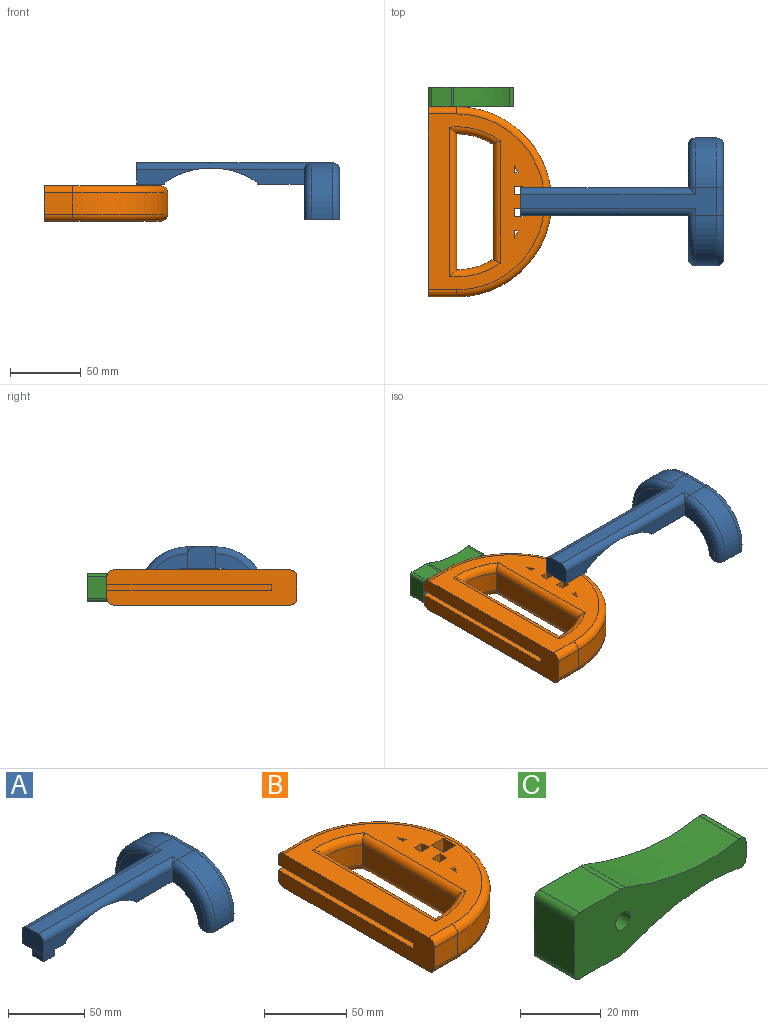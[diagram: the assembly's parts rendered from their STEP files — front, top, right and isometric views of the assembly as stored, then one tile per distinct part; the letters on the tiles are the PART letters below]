
ASSEMBLY  parts=3 mates=2
PART A: 36 faces, bbox 143.8x96.2x43.9 mm
  f0: plane 20x19.96mm, normal (0,0,-1), area 299.2mm2, adj f1,f2,f3,f7,f31,f32,f33,f34
  f1: plane 40.31x10mm, normal (0,1,0), area 274.9mm2, adj f0,f3,f7,f18,f28
  f2: plane 40.31x10mm, normal (0,-1,0), area 274.9mm2, adj f0,f3,f7,f18,f25
  f3: plane 20x1mm, normal (1,0,0), area 20mm2, adj f0,f1,f2,f18
  f4: plane 53.52x10mm, normal (0,-1,0), area 407mm2, adj f6,f11,f18,f19,f25
  f5: plane 53.52x10mm, normal (0,1,0), area 407mm2, adj f6,f17,f18,f19,f28
  f6: plane 58.17x20mm, normal (0,0,-1), area 1163.4mm2, adj f4,f5,f8,f12,f14,f19
  f7: plane 20x15mm, normal (-1,0,0), area 289.3mm2, adj f0,f1,f2,f9,f25,f28
  f8: plane 80.39x34.78mm, normal (1,0,0), area 932.2mm2, adj f6,f10,f12,f14,f15,f20,f21,f22
  f9: plane 138.77x20mm, normal (0,0,1), area 1537.7mm2, adj f7,f13,f16,f21,f25,f26,f28,f29
  f10: plane 25x5.44mm, normal (0,0,-1), area 125.2mm2, adj f8,f11,f13,f20,f24,f27
  f11: plane 34.78x30.2mm, normal (-1,0,0), area 366.1mm2, adj f4,f10,f12,f24,f27
  f12: cylinder r=24.9mm len=25mm, axis (1,0,0), area 870.7mm2, adj f6,f8,f11,f24
  f13: cylinder r=35.2mm len=39.78mm, axis (1,0,0), area 898.3mm2, adj f9,f10,f20,f27
  f14: cylinder r=24.9mm len=25mm, axis (1,0,0), area 870.7mm2, adj f6,f8,f17,f23
  f15: plane 25x5.44mm, normal (0,0,-1), area 125.2mm2, adj f8,f16,f17,f22,f23,f30
  f16: cylinder r=35.2mm len=39.78mm, axis (1,0,0), area 898.3mm2, adj f9,f15,f22,f30
  f17: plane 34.78x30.2mm, normal (-1,0,0), area 366.1mm2, adj f5,f14,f15,f23,f30
  f18: cylinder r=57.08mm len=65.64mm, axis (0,1,0), area 1393.5mm2, adj f1,f2,f3,f4,f5,f19,f25,f28
  f19: plane 20x1mm, normal (-1,0,0), area 20mm2, adj f4,f5,f6,f18
  f20: torus R=30.2mm, axis (1,0,0), area 448mm2, adj f8,f10,f13,f21
  f21: cylinder r=5mm len=20mm, axis (0,-1,0), area 157.1mm2, adj f8,f9,f20,f22
  f22: torus R=30.2mm, axis (1,0,0), area 448mm2, adj f8,f15,f16,f21
  f23: cylinder r=5mm len=25mm, axis (1,0,0), area 174.9mm2, adj f8,f14,f15,f17
  f24: cylinder r=5mm len=25mm, axis (1,0,0), area 174.9mm2, adj f8,f10,f11,f12
  f25: cylinder r=5mm len=123.77mm, axis (-1,0,0), area 923.9mm2, adj f2,f4,f7,f9,f18,f26
  f26: cylinder r=5mm len=5mm, axis (0,-1,0), area 14.3mm2, adj f9,f25,f27
  f27: torus R=30.2mm, axis (1,0,0), area 448mm2, adj f10,f11,f13,f26
  f28: cylinder r=5mm len=123.77mm, axis (1,0,0), area 923.9mm2, adj f1,f5,f7,f9,f18,f29
  f29: cylinder r=5mm len=5mm, axis (0,1,0), area 14.3mm2, adj f9,f28,f30
  f30: torus R=30.2mm, axis (1,0,0), area 448mm2, adj f15,f16,f17,f29
  f31: plane 10x10mm, normal (0,-1,0), area 100mm2, adj f0,f32,f34,f35
  f32: plane 10x10mm, normal (-1,0,0), area 100mm2, adj f0,f31,f33,f35
  f33: plane 10x10mm, normal (0,1,0), area 100mm2, adj f0,f32,f34,f35
  f34: plane 10x10mm, normal (1,0,0), area 100mm2, adj f0,f31,f33,f35
  f35: plane 10x10mm, normal (0,0,-1), area 100mm2, adj f31,f32,f33,f34
PART B: 51 faces, bbox 92.8x145.7x25 mm
  f0: plane 124.58x82.25mm, normal (0,0,1), area 4768.2mm2, adj f2,f3,f4,f5,f7,f8,f11,f15
  f1: plane 19.96x15mm, normal (0,1,0), area 246.8mm2, adj f10,f11,f15,f20,f32,f40,f41,f42
  f2: plane 25x5.55mm, normal (1,0,0), area 138.8mm2, adj f0,f14,f21,f29
  f3: cylinder r=48.18mm len=25mm, axis (0,0,-1), area 140.7mm2, adj f0,f14,f21,f29
  f4: plane 25x5.62mm, normal (1,0,0), area 140.4mm2, adj f0,f14,f27,f28
  f5: cylinder r=48.18mm len=25mm, axis (0,0,-1), area 143.1mm2, adj f0,f14,f22,f23
  f6: cylinder r=48.18mm len=25.79mm, axis (0,0,-1), area 408.3mm2, adj f9,f24,f36,f39
  f7: cylinder r=48.18mm len=25mm, axis (0,0,-1), area 145.2mm2, adj f0,f14,f25,f26
  f8: cylinder r=48.18mm len=25mm, axis (0,0,-1), area 142.4mm2, adj f0,f14,f27,f28
  f9: plane 96.37x15mm, normal (1,0,0), area 1445.5mm2, adj f6,f13,f35,f38
  f10: cylinder r=67.29mm len=134.58mm, axis (0,0,-1), area 3170.9mm2, adj f1,f12,f16,f19
  f11: plane 134.58x25mm, normal (-1,0,0), area 2875.8mm2, adj f0,f1,f12,f14,f15,f17,f18,f20
  f12: plane 19.96x15mm, normal (0,-1,0), area 299.4mm2, adj f10,f11,f17,f18
  f13: cylinder r=48.18mm len=25.79mm, axis (0,0,-1), area 408.3mm2, adj f9,f24,f34,f37
  f14: plane 124.58x82.25mm, normal (0,0,-1), area 4878.4mm2, adj f2,f3,f4,f5,f7,f8,f11,f18
  f15: cylinder r=5mm len=19.96mm, axis (1,0,0), area 156.8mm2, adj f0,f1,f11,f16
  f16: torus R=62.29mm, axis (0,0,1), area 1615.5mm2, adj f0,f10,f15,f17
  f17: cylinder r=5mm len=19.96mm, axis (-1,0,0), area 156.8mm2, adj f0,f11,f12,f16
  f18: cylinder r=5mm len=19.96mm, axis (1,0,0), area 156.8mm2, adj f11,f12,f14,f19
  f19: torus R=62.29mm, axis (0,0,1), area 1615.5mm2, adj f10,f14,f18,f20
  f20: cylinder r=5mm len=19.96mm, axis (-1,0,0), area 156.8mm2, adj f1,f11,f14,f19
  f21: plane 25x6.2mm, normal (0,-1,0), area 155mm2, adj f0,f2,f3,f14
  f22: plane 25x2.75mm, normal (0,1,0), area 68.8mm2, adj f0,f5,f14,f23
  f23: plane 25x5.02mm, normal (1,0,0), area 125.4mm2, adj f0,f5,f14,f22
  f24: plane 81.39x15mm, normal (-1,0,0), area 1220.9mm2, adj f6,f13,f30,f31
  f25: plane 25x5.09mm, normal (1,0,0), area 127.3mm2, adj f0,f7,f14,f26
  f26: plane 25x2.79mm, normal (0,-1,0), area 69.7mm2, adj f0,f7,f14,f25
  f27: plane 25x6.22mm, normal (0,1,0), area 155.5mm2, adj f0,f4,f8,f14
  f28: plane 25x7.13mm, normal (0,-1,0), area 178.4mm2, adj f0,f4,f8,f14
  f29: plane 25x7.12mm, normal (0,1,0), area 178mm2, adj f0,f2,f3,f14
  f30: cylinder r=5mm len=86.72mm, axis (0,-1,0), area 654.6mm2, adj f14,f24,f34,f36
  f31: cylinder r=5mm len=86.72mm, axis (0,1,0), area 654.6mm2, adj f0,f24,f37,f39
  f32: cylinder r=2.5mm len=5mm, axis (0,-1,0), area 78.5mm2, adj f1,f33
  f33: plane 5x5mm, normal (0,1,0), area 19.6mm2, adj f32
  f34: torus R=53.18mm, axis (0,0,1), area 244.1mm2, adj f13,f14,f30,f35
  f35: cylinder r=5mm len=105.89mm, axis (0,1,0), area 784.5mm2, adj f9,f14,f34,f36
  f36: torus R=53.18mm, axis (0,0,1), area 244.1mm2, adj f6,f14,f30,f35
  f37: torus R=53.18mm, axis (0,0,1), area 244.1mm2, adj f0,f13,f31,f38
  f38: cylinder r=5mm len=105.89mm, axis (0,-1,0), area 784.5mm2, adj f0,f9,f37,f39
  f39: torus R=53.18mm, axis (0,0,1), area 244.1mm2, adj f0,f6,f31,f38
  f40: plane 116.8x5mm, normal (0,0,-1), area 584mm2, adj f1,f11,f41,f45
  f41: plane 116.8x2.12mm, normal (0.71,0,-0.71), area 350.4mm2, adj f1,f40,f42,f45
  f42: plane 116.8x8.24mm, normal (-1,0,0), area 962.7mm2, adj f1,f41,f43,f45
  f43: plane 116.8x2.12mm, normal (0.71,0,0.71), area 350.4mm2, adj f1,f42,f44,f45
  f44: plane 116.8x5mm, normal (0,0,1), area 584mm2, adj f1,f11,f43,f45
  f45: plane 8.24x7.12mm, normal (0,1,0), area 33mm2, adj f11,f40,f41,f42,f43,f44
  f46: plane 10.5x10mm, normal (0,-1,0), area 105mm2, adj f0,f47,f49,f50
  f47: plane 10.5x10mm, normal (1,0,0), area 105mm2, adj f0,f46,f48,f50
  f48: plane 10.5x10mm, normal (0,1,0), area 105mm2, adj f0,f47,f49,f50
  f49: plane 10.5x10mm, normal (-1,0,0), area 105mm2, adj f0,f46,f48,f50
  f50: plane 10.5x10.5mm, normal (0,0,1), area 110.3mm2, adj f46,f47,f48,f49
PART C: 16 faces, bbox 60.1x14x20 mm
  f0: plane 60.09x20mm, normal (0,1,0), area 776.8mm2, adj f2,f3,f4,f7,f8,f9,f10,f11
  f1: plane 60.09x20mm, normal (0,-1,0), area 756.4mm2, adj f2,f3,f4,f5,f7,f8,f9,f10
  f2: plane 14x4.92mm, normal (1,0,0), area 68.9mm2, adj f0,f1,f9,f10
  f3: plane 14.11x14mm, normal (0,0,1), area 197.6mm2, adj f0,f1,f12,f15
  f4: plane 14.11x14mm, normal (0,0,-1), area 197.6mm2, adj f0,f1,f13,f14
  f5: cylinder r=2.55mm len=5.1mm, axis (0,-1,0), area 80.1mm2, adj f1,f6
  f6: plane 5.1x5.1mm, normal (0,-1,0), area 20.4mm2, adj f5
  f7: extruded ~39.7x14mm, area 568.8mm2, adj f0,f1,f10,f15
  f8: extruded ~39.7x14mm, area 568.8mm2, adj f0,f1,f9,f14
  f9: cylinder r=2mm len=14mm, axis (0,1,0), area 49.9mm2, adj f0,f1,f2,f8
  f10: cylinder r=2mm len=14mm, axis (0,1,0), area 49.9mm2, adj f0,f1,f2,f7
  f11: plane 16x14mm, normal (-1,0,0), area 224mm2, adj f0,f1,f12,f13
  f12: cylinder r=2mm len=14mm, axis (0,1,0), area 44mm2, adj f0,f1,f3,f11
  f13: cylinder r=2mm len=14mm, axis (0,-1,0), area 44mm2, adj f0,f1,f4,f11
  f14: cylinder r=5mm len=14mm, axis (0,1,0), area 26.6mm2, adj f0,f1,f4,f8
  f15: cylinder r=5mm len=14mm, axis (0,1,0), area 26.6mm2, adj f0,f1,f3,f7
PLACE A t=(-363.17,-121.44,-156.49)mm
PLACE B t=(-428.39,-121.44,-157.79)mm
PLACE C t=(-464.25,-54.22,-67.69)mm
MATE revolute C.f5 <-> B.f32  axis (0,-1,0) through (-454.25,-49.22,-157.79)mm
MATE slider B.f50 <-> A.f35  axis (0,0,1) through (-396.14,-121.44,-155.29)mm
